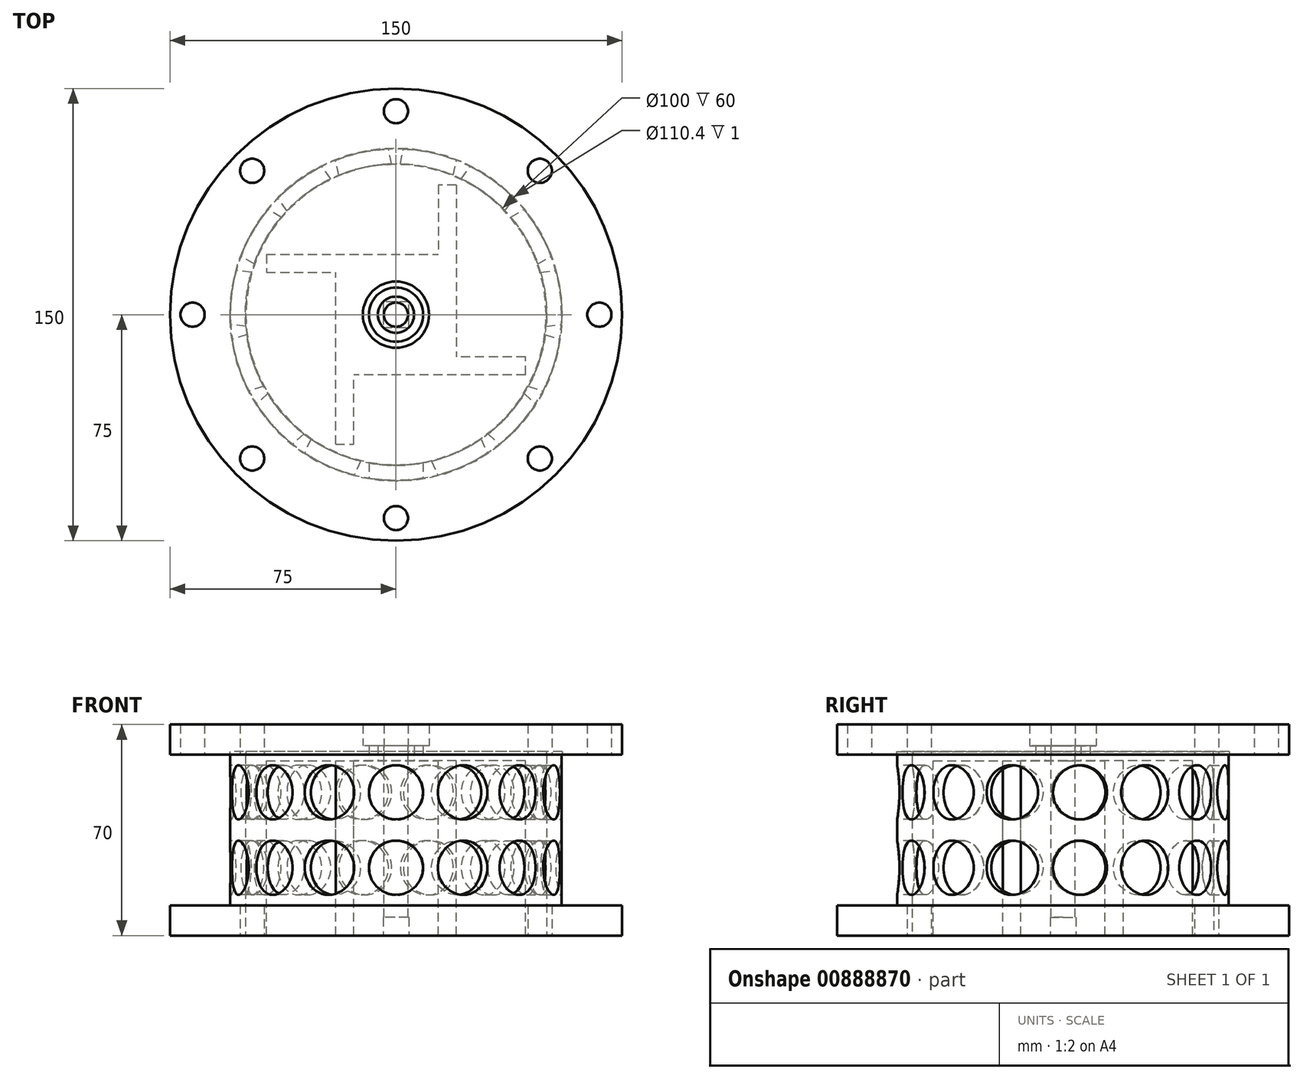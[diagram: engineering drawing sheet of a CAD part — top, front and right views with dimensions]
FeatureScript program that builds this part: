
annotation { "Feature Type Name" : "Feature", "Feature Type Description" : "" }
export const myFeature = defineFeature(function(context is Context, id is Id, definition is map)
    precondition{}
    {
        {
            var Q0;
            Q0=qCreatedBy(makeId("Top.planeOp"),FACE);
            cPlane(context, id + "F0", {"entities" : qUnion([Q0]), "cplaneType" : CPlaneType.OFFSET, "offset" : 60 * mm, "oppositeDirection" : true, "width" : 150 * mm, "height" : 150 * mm});
        }
        {
            var Q0;
            Q0=qCreatedBy(makeId("Top.planeOp"),FACE);
            cPlane(context, id + "F1", {"entities" : qUnion([Q0]), "cplaneType" : CPlaneType.OFFSET, "offset" : 2 * mm, "oppositeDirection" : true, "width" : 150 * mm, "height" : 150 * mm});
        }
        {
            var Q0;
            Q0=qCreatedBy(makeId("Front.planeOp"),FACE);
            cPlane(context, id + "F2", {"entities" : qUnion([Q0]), "cplaneType" : CPlaneType.OFFSET, "offset" : 55 * mm, "width" : 150 * mm, "height" : 150 * mm});
        }
        {
            var Q0;
            Q0=qCreatedBy(makeId("Top.planeOp"),FACE);
            var sketch = newSketch(context, id + "F3", { "sketchPlane" : qUnion([Q0])});
            skCircle(sketch, "E0", {"center": v(0, 0) * mm, "radius": 75 * mm});
            skCircle(sketch, "E1", {"center": v(0, 0) * mm, "radius": 67.5 * mm, "construction": true});
            skCircle(sketch, "E2", {"center": v(0, 67.5) * mm, "radius": 4 * mm});
            skCircle(sketch, "E3.1.1", {"center": v(-47.73, 47.73) * mm, "radius": 4 * mm});
            skCircle(sketch, "E3.2.1", {"center": v(-67.5, 0) * mm, "radius": 4 * mm});
            skCircle(sketch, "E3.3.1", {"center": v(-47.73, -47.73) * mm, "radius": 4 * mm});
            skCircle(sketch, "E3.4.1", {"center": v(0, -67.5) * mm, "radius": 4 * mm});
            skCircle(sketch, "E3.5.1", {"center": v(47.73, -47.73) * mm, "radius": 4 * mm});
            skCircle(sketch, "E3.6.1", {"center": v(67.5, 0) * mm, "radius": 4 * mm});
            skCircle(sketch, "E3.7.1", {"center": v(47.73, 47.73) * mm, "radius": 4 * mm});
            skCircle(sketch, "E4", {"center": v(0, 0) * mm, "radius": 11 * mm});
            skSolve(sketch);
        }
        {
            var Q0;
            Q0=qSketchRegion(id+"F3",true);
            var Q1;
            Q1=makeQuery(id+"F3.imprint","IMPRINT",FACE,{"disambiguationData":[TD([[makeQuery(id+"F3.imprint","IMPRINT",EDGE,{"derivedFrom":sQuery(id+"F3.wireOp",EDGE,"E4")}),-1.0]])]});
            extrude(context, id + "F4", {"entities" : qUnion([Q0, Q1]), "depth" : 10 * mm, "offsetDistance" : 25 * mm});
        }
        {
            var Q0;
            Q0=qCreatedBy(id+"F0.planeOp",FACE);
            var sketch = newSketch(context, id + "F5", { "sketchPlane" : qUnion([Q0])});
            skCircle(sketch, "E5.0", {"center": v(0, 0) * mm, "radius": 75 * mm});
            skCircle(sketch, "E6.0", {"center": v(-47.73, 47.73) * mm, "radius": 4 * mm});
            skCircle(sketch, "E7.0", {"center": v(-47.73, -47.73) * mm, "radius": 4 * mm});
            skCircle(sketch, "E8.0", {"center": v(47.73, -47.73) * mm, "radius": 4 * mm});
            skCircle(sketch, "E9.0", {"center": v(47.73, 47.73) * mm, "radius": 4 * mm});
            skCircle(sketch, "E10", {"center": v(0, 0) * mm, "radius": 55 * mm});
            skCircle(sketch, "E11", {"center": v(0, 0) * mm, "radius": 50 * mm});
            skSolve(sketch);
        }
        {
            var Q0;
            Q0=makeQuery(id+"F5.imprint","IMPRINT",FACE,{"disambiguationData":[TD([[makeQuery(id+"F5.imprint","IMPRINT",EDGE,{"derivedFrom":sQuery(id+"F5.wireOp",EDGE,"E10")}),1.0]])]});
            extrude(context, id + "F6", {"entities" : qUnion([Q0]), "depth" : 60 * mm, "offsetDistance" : 25 * mm});
        }
        {
            var Q0;
            Q0=qSketchRegion(id+"F5",true);
            extrude(context, id + "F7", {"entities" : qUnion([Q0]), "operationType" : NewBodyOperationType.ADD, "depth" : 10 * mm, "offsetDistance" : 25 * mm});
        }
        {
            var Q0;
            Q0=qCreatedBy(id+"F1.planeOp",FACE);
            var sketch = newSketch(context, id + "F8", { "sketchPlane" : qUnion([Q0])});
            skCircle(sketch, "E12.0", {"center": v(0, 0) * mm, "radius": 50 * mm, "construction": true});
            skLineSegment(sketch, "E13", {"start": v(0, 42.18) * mm, "end": v(0, -43.72) * mm, "construction": true});
            skCircle(sketch, "E14", {"center": v(0, 0) * mm, "radius": 4 * mm});
            skCircle(sketch, "E15.cCircle", {"center": v(0, 0) * mm, "radius": 20 * mm, "construction": true});
            skLineSegment(sketch, "E15.0", {"start": v(-20, 20) * mm, "end": v(14, 20) * mm});
            skLineSegment(sketch, "E15.1", {"start": v(20, 20) * mm, "end": v(20, -14) * mm});
            skLineSegment(sketch, "E15.2", {"start": v(20, -20) * mm, "end": v(-14, -20) * mm});
            skLineSegment(sketch, "E15.3", {"start": v(-20, -20) * mm, "end": v(-20, 14) * mm});
            skPoint(sketch, "E15.0.midPoint", {"position": v(0, 20) * mm});
            skLineSegment(sketch, "E16", {"start": v(20, 20) * mm, "end": v(20, 43) * mm});
            skLineSegment(sketch, "E17", {"start": v(20, 43) * mm, "end": v(14, 43) * mm});
            skLineSegment(sketch, "E18", {"start": v(14, 43) * mm, "end": v(14, 20) * mm});
            skLineSegment(sketch, "E19.1.0", {"start": v(-20, 20) * mm, "end": v(-43, 20) * mm});
            skLineSegment(sketch, "E19.1.1", {"start": v(-43, 14) * mm, "end": v(-20, 14) * mm});
            skLineSegment(sketch, "E19.1.2", {"start": v(-43, 20) * mm, "end": v(-43, 14) * mm});
            skLineSegment(sketch, "E19.2.0", {"start": v(-20, -20) * mm, "end": v(-20, -43) * mm});
            skLineSegment(sketch, "E19.2.1", {"start": v(-14, -43) * mm, "end": v(-14, -20) * mm});
            skLineSegment(sketch, "E19.2.2", {"start": v(-20, -43) * mm, "end": v(-14, -43) * mm});
            skLineSegment(sketch, "E19.3.0", {"start": v(20, -20) * mm, "end": v(43, -20) * mm});
            skLineSegment(sketch, "E19.3.1", {"start": v(43, -14) * mm, "end": v(20, -14) * mm});
            skLineSegment(sketch, "E19.3.2", {"start": v(43, -20) * mm, "end": v(43, -14) * mm});
            skSolve(sketch);
        }
        {
            var Q0;
            Q0=qSketchRegion(id+"F8",true);
            extrude(context, id + "F9", {"entities" : qUnion([Q0]), "oppositeDirection" : true, "depth" : 58 * mm, "offsetDistance" : 25 * mm});
        }
        {
            var Q0;
            Q0=qCreatedBy(id+"F2.planeOp",FACE);
            var sketch = newSketch(context, id + "F10", { "sketchPlane" : qUnion([Q0])});
            skLineSegment(sketch, "E20", {"start": v(-55, -25) * mm, "end": v(-55, 0) * mm, "construction": true});
            skLineSegment(sketch, "E21", {"start": v(55, 0) * mm, "end": v(55, -25) * mm, "construction": true});
            skLineSegment(sketch, "E22", {"start": v(-75, 0) * mm, "end": v(-75, 10) * mm, "construction": true});
            skLineSegment(sketch, "E23", {"start": v(75, 10) * mm, "end": v(75, 0) * mm, "construction": true});
            skLineSegment(sketch, "E24", {"start": v(-55, 0) * mm, "end": v(55, -25) * mm, "construction": true});
            skLineSegment(sketch, "E25", {"start": v(55, 0) * mm, "end": v(-55, -25) * mm, "construction": true});
            skCircle(sketch, "E26", {"center": v(0, -12.5) * mm, "radius": 9 * mm});
            skCircle(sketch, "E27", {"center": v(0, -37.5) * mm, "radius": 9 * mm});
            skLineSegment(sketch, "E28", {"start": v(-75, -60) * mm, "end": v(-75, -50) * mm, "construction": true});
            skLineSegment(sketch, "E29", {"start": v(75, -50) * mm, "end": v(75, -60) * mm, "construction": true});
            skLineSegment(sketch, "E30", {"start": v(75, -50) * mm, "end": v(-32.41, -50) * mm, "construction": true});
            skSolve(sketch);
        }
        {
            var Q0;
            Q0=qSketchRegion(id+"F10",true);
            extrude(context, id + "F11", {"entities" : qUnion([Q0]), "oppositeDirection" : true, "depth" : 7 * mm, "offsetDistance" : 25 * mm});
        }
        {
            var Q0;
            Q0=makeQuery(id+"F11.opExtrude","SWEPT_BODY",BODY,{"disambiguationData":[OSD([sQuery(id+"F10.wireOp",EDGE,"E26")])]});
            var Q1;
            Q1=makeQuery(id+"F11.opExtrude","SWEPT_BODY",BODY,{"disambiguationData":[OSD([sQuery(id+"F10.wireOp",EDGE,"E27")])]});
            var Q2;
            Q2=makeQuery(id+"F7.opExtrude","CAP_EDGE",EDGE,{"disambiguationData":[OSD([sQuery(id+"F5.wireOp",EDGE,"E5.0")])],"isStart":false});
            circularPattern(context, id + "F12", {"operationType" : NewBodyOperationType.REMOVE, "entities" : qUnion([Q0, Q1]), "axis" : qUnion([Q2]), "angle" : 360 * degree, "instanceCount" : 15, "equalSpace" : true});
        }
        {
            var Q0;
            Q0=qCreatedBy(makeId("Top.planeOp"),FACE);
            var sketch = newSketch(context, id + "F13", { "sketchPlane" : qUnion([Q0])});
            skCircle(sketch, "E31.0", {"center": v(0, 0) * mm, "radius": 50 * mm, "construction": true});
            skCircle(sketch, "E32.0", {"center": v(0, 0) * mm, "radius": 55 * mm, "construction": true});
            skCircle(sketch, "E33.0", {"center": v(0, 0) * mm, "radius": 55.2 * mm});
            skCircle(sketch, "E34.0", {"center": v(0, 0) * mm, "radius": 49.8 * mm});
            skSolve(sketch);
        }
        {
            var Q0;
            Q0=qSketchRegion(id+"F13",true);
            extrude(context, id + "F14", {"entities" : qUnion([Q0]), "operationType" : NewBodyOperationType.REMOVE, "depth" : 1 * mm, "offsetDistance" : 25 * mm});
        }
        {
            var Q0;
            Q0=qCreatedBy(makeId("Top.planeOp"),FACE);
            var sketch = newSketch(context, id + "F15", { "sketchPlane" : qUnion([Q0])});
            skCircle(sketch, "E35.0", {"center": v(0, 0) * mm, "radius": 11 * mm});
            skCircle(sketch, "E36", {"center": v(0, 0) * mm, "radius": 9 * mm});
            skSolve(sketch);
        }
        {
            var Q0;
            Q0=qSketchRegion(id+"F15",true);
            extrude(context, id + "F16", {"entities" : qUnion([Q0]), "operationType" : NewBodyOperationType.ADD, "depth" : 3 * mm, "offsetDistance" : 25 * mm});
        }
        {
            var Q0;
            Q0=makeQuery(id+"F9.opExtrude","CAP_FACE",FACE,{"disambiguationData":[OSD([sQuery(id+"F8.wireOp",EDGE,"E14"),sQuery(id+"F8.wireOp",EDGE,"E15.0"),sQuery(id+"F8.wireOp",EDGE,"E15.1"),sQuery(id+"F8.wireOp",EDGE,"E15.2"),sQuery(id+"F8.wireOp",EDGE,"E15.3"),sQuery(id+"F8.wireOp",EDGE,"E16"),sQuery(id+"F8.wireOp",EDGE,"E17"),sQuery(id+"F8.wireOp",EDGE,"E18"),sQuery(id+"F8.wireOp",EDGE,"E19.1.0"),sQuery(id+"F8.wireOp",EDGE,"E19.1.1"),sQuery(id+"F8.wireOp",EDGE,"E19.1.2"),sQuery(id+"F8.wireOp",EDGE,"E19.2.0"),sQuery(id+"F8.wireOp",EDGE,"E19.2.1"),sQuery(id+"F8.wireOp",EDGE,"E19.2.2"),sQuery(id+"F8.wireOp",EDGE,"E19.3.0"),sQuery(id+"F8.wireOp",EDGE,"E19.3.1"),sQuery(id+"F8.wireOp",EDGE,"E19.3.2")])],"isStart":false});
            var sketch = newSketch(context, id + "F17", { "sketchPlane" : qUnion([Q0])});
            skCircle(sketch, "E37.cCircle", {"center": v(0, 0) * mm, "radius": 4.25 * mm, "construction": true});
            skLineSegment(sketch, "E37.0", {"start": v(4.25, -4.25) * mm, "end": v(-4.25, -4.25) * mm});
            skLineSegment(sketch, "E37.1", {"start": v(-4.25, -4.25) * mm, "end": v(-4.25, 4.25) * mm});
            skLineSegment(sketch, "E37.2", {"start": v(-4.25, 4.25) * mm, "end": v(4.25, 4.25) * mm});
            skLineSegment(sketch, "E37.3", {"start": v(4.25, 4.25) * mm, "end": v(4.25, -4.25) * mm});
            skPoint(sketch, "E37.0.midPoint", {"position": v(0, -4.25) * mm});
            skSolve(sketch);
        }
        {
            var Q0;
            Q0=qSketchRegion(id+"F17",true);
            extrude(context, id + "F18", {"entities" : qUnion([Q0]), "operationType" : NewBodyOperationType.REMOVE, "oppositeDirection" : true, "depth" : 6 * mm, "offsetDistance" : 25 * mm});
        }
        {
            var Q0;
            Q0=makeQuery(id+"F9.opExtrude","CAP_FACE",FACE,{"disambiguationData":[OSD([sQuery(id+"F8.wireOp",EDGE,"E14"),sQuery(id+"F8.wireOp",EDGE,"E15.0"),sQuery(id+"F8.wireOp",EDGE,"E15.1"),sQuery(id+"F8.wireOp",EDGE,"E15.2"),sQuery(id+"F8.wireOp",EDGE,"E15.3"),sQuery(id+"F8.wireOp",EDGE,"E16"),sQuery(id+"F8.wireOp",EDGE,"E17"),sQuery(id+"F8.wireOp",EDGE,"E18"),sQuery(id+"F8.wireOp",EDGE,"E19.1.0"),sQuery(id+"F8.wireOp",EDGE,"E19.1.1"),sQuery(id+"F8.wireOp",EDGE,"E19.1.2"),sQuery(id+"F8.wireOp",EDGE,"E19.2.0"),sQuery(id+"F8.wireOp",EDGE,"E19.2.1"),sQuery(id+"F8.wireOp",EDGE,"E19.2.2"),sQuery(id+"F8.wireOp",EDGE,"E19.3.0"),sQuery(id+"F8.wireOp",EDGE,"E19.3.1"),sQuery(id+"F8.wireOp",EDGE,"E19.3.2")])],"isStart":true});
            var sketch = newSketch(context, id + "F19", { "sketchPlane" : qUnion([Q0])});
            skCircle(sketch, "E38", {"center": v(0, 0) * mm, "radius": 6 * mm});
            skCircle(sketch, "E39.0", {"center": v(0, 0) * mm, "radius": 4 * mm});
            skSolve(sketch);
        }
        {
            var Q0;
            Q0=qSketchRegion(id+"F19",true);
            extrude(context, id + "F20", {"entities" : qUnion([Q0]), "operationType" : NewBodyOperationType.ADD, "depth" : 5 * mm, "offsetDistance" : 25 * mm});
        }
    });
